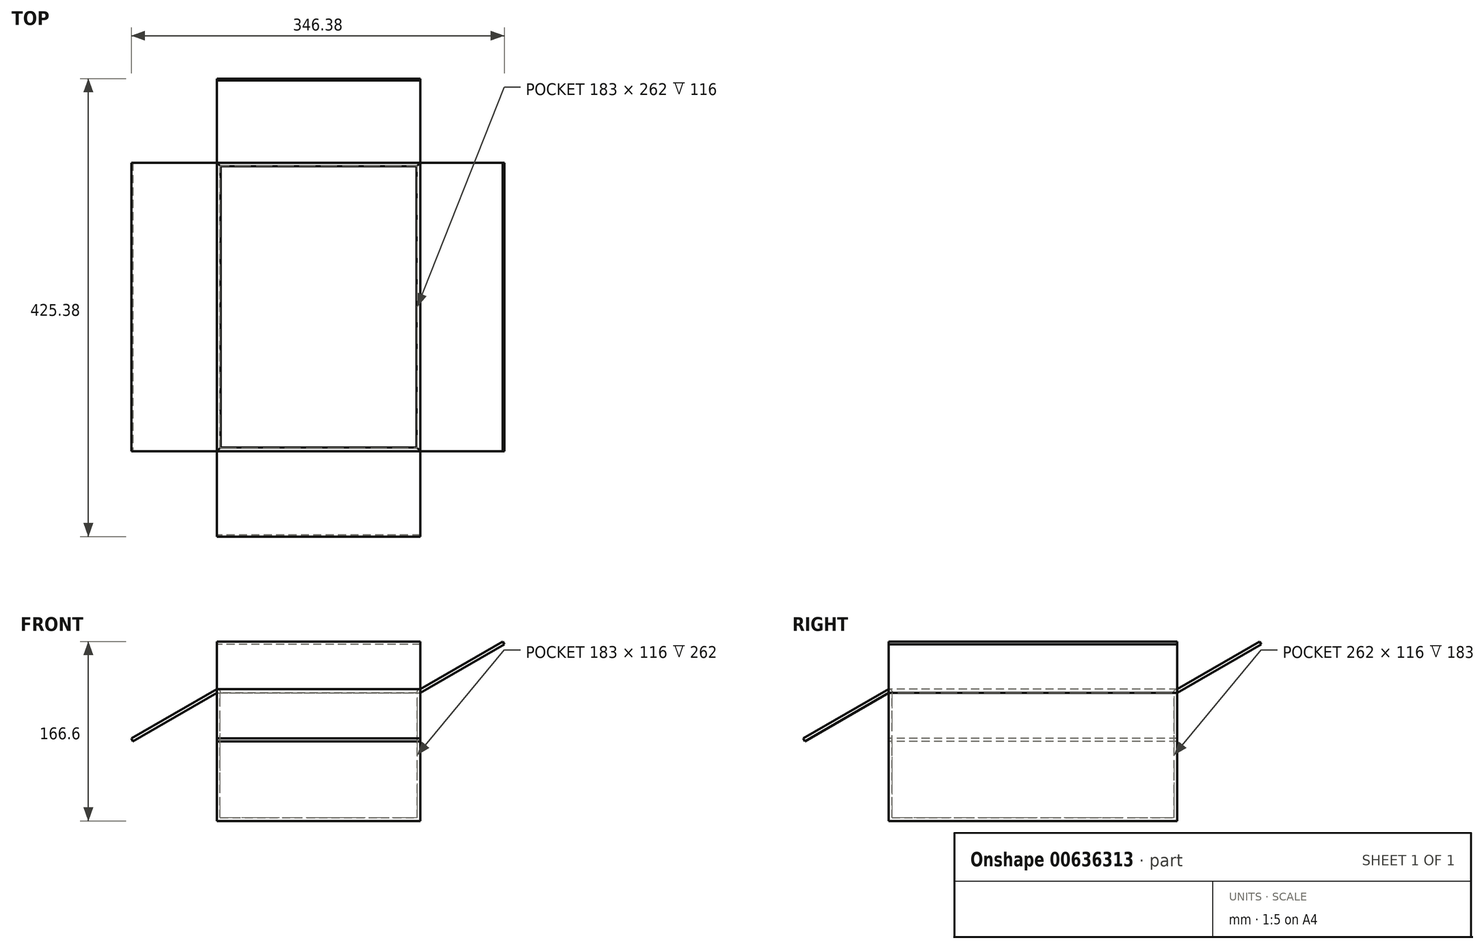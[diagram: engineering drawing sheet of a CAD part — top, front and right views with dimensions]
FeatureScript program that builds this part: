
annotation { "Feature Type Name" : "Feature", "Feature Type Description" : "" }
export const myFeature = defineFeature(function(context is Context, id is Id, definition is map)
    precondition{}
    {
        {
            var Q0;
            Q0=qCreatedBy(makeId("Front.planeOp"),FACE);
            var sketch = newSketch(context, id + "F0", { "sketchPlane" : qUnion([Q0])});
            skLineSegment(sketch, "E0.bottom", {"start": v(0, 0) * mm, "end": v(189, 0) * mm});
            skLineSegment(sketch, "E0.top", {"start": v(0, 119) * mm, "end": v(189, 119) * mm});
            skLineSegment(sketch, "E0.left", {"start": v(0, 0) * mm, "end": v(0, 119) * mm});
            skLineSegment(sketch, "E0.right", {"start": v(189, 0) * mm, "end": v(189, 119) * mm});
            skSolve(sketch);
        }
        {
            var Q0;
            Q0=qSketchRegion(id+"F0",true);
            extrude(context, id + "F1", {"entities" : qUnion([Q0]), "depth" : 268 * mm, "offsetDistance" : 25 * mm});
        }
        {
            var Q0;
            Q0=makeQuery(id+"F1.opExtrude","SWEPT_FACE",FACE,{"disambiguationData":[OSD([sQuery(id+"F0.wireOp",EDGE,"E0.top")])]});
            shell(context, id + "F2", {"entities" : qUnion([Q0]), "thickness" : 3 * mm});
        }
        {
            var Q0;
            Q0=makeQuery(id+"F1.opExtrude","CAP_FACE",FACE,{"disambiguationData":[OSD([sQuery(id+"F0.wireOp",EDGE,"E0.bottom"),sQuery(id+"F0.wireOp",EDGE,"E0.top"),sQuery(id+"F0.wireOp",EDGE,"E0.left"),sQuery(id+"F0.wireOp",EDGE,"E0.right")])],"isStart":false});
            var sketch = newSketch(context, id + "F3", { "sketchPlane" : qUnion([Q0])});
            skLineSegment(sketch, "E1", {"start": v(0, 119) * mm, "end": v(-77.94, 74) * mm});
            skLineSegment(sketch, "E2", {"start": v(-77.94, 74) * mm, "end": v(-79.44, 76.6) * mm});
            skLineSegment(sketch, "E3", {"start": v(-79.44, 76.6) * mm, "end": v(0, 122.46) * mm});
            skArc(sketch, "E4", {"start": v(0, 122.46) * mm, "mid": v(2.45, 121.45) * mm, "end": v(3.46, 119) * mm});
            skLineSegment(sketch, "E5", {"start": v(189, 119) * mm, "end": v(266.94, 164) * mm});
            skLineSegment(sketch, "E6", {"start": v(266.94, 164) * mm, "end": v(265.44, 166.6) * mm});
            skLineSegment(sketch, "E7", {"start": v(265.44, 166.6) * mm, "end": v(189, 122.46) * mm});
            skArc(sketch, "E8", {"start": v(189, 122.46) * mm, "mid": v(186.55, 121.45) * mm, "end": v(185.54, 119) * mm});
            skLineSegment(sketch, "E9", {"start": v(0, 119) * mm, "end": v(3.46, 119) * mm});
            skLineSegment(sketch, "E10", {"start": v(185.54, 119) * mm, "end": v(189, 119) * mm});
            skSolve(sketch);
        }
        {
            var Q0;
            Q0=qSketchRegion(id+"F3",true);
            var Q1;
            Q1=makeQuery(id+"F1.opExtrude","CAP_FACE",FACE,{"disambiguationData":[OSD([sQuery(id+"F0.wireOp",EDGE,"E0.bottom"),sQuery(id+"F0.wireOp",EDGE,"E0.top"),sQuery(id+"F0.wireOp",EDGE,"E0.left"),sQuery(id+"F0.wireOp",EDGE,"E0.right")])],"isStart":true});
            extrude(context, id + "F4", {"entities" : qUnion([Q0]), "operationType" : NewBodyOperationType.ADD, "endBound" : BoundingType.UP_TO_SURFACE, "oppositeDirection" : true, "depth" : 216 * mm, "endBoundEntityFace" : qUnion([Q1]), "offsetDistance" : 25 * mm});
        }
        {
            var Q0;
            Q0=makeQuery(id+"F1.opExtrude","SWEPT_FACE",FACE,{"disambiguationData":[OSD([sQuery(id+"F0.wireOp",EDGE,"E0.left")])]});
            var sketch = newSketch(context, id + "F5", { "sketchPlane" : qUnion([Q0])});
            skLineSegment(sketch, "E11", {"start": v(268, 119) * mm, "end": v(345.94, 74) * mm});
            skLineSegment(sketch, "E12", {"start": v(345.94, 74) * mm, "end": v(347.44, 76.6) * mm});
            skLineSegment(sketch, "E13", {"start": v(0, 119) * mm, "end": v(-77.94, 164) * mm});
            skLineSegment(sketch, "E14", {"start": v(-77.94, 164) * mm, "end": v(-76.44, 166.6) * mm});
            skLineSegment(sketch, "E15", {"start": v(-76.44, 166.6) * mm, "end": v(0, 122.46) * mm});
            skArc(sketch, "E16", {"start": v(0, 122.46) * mm, "mid": v(2.45, 121.45) * mm, "end": v(3.46, 119) * mm});
            skLineSegment(sketch, "E17", {"start": v(0, 119) * mm, "end": v(3.46, 119) * mm});
            skPoint(sketch, "E18.0", {"position": v(268, 122.46) * mm});
            skArc(sketch, "E19", {"start": v(268, 122.46) * mm, "mid": v(265.55, 121.45) * mm, "end": v(264.54, 119) * mm});
            skLineSegment(sketch, "E20", {"start": v(264.54, 119) * mm, "end": v(268, 119) * mm});
            skLineSegment(sketch, "E21", {"start": v(268, 122.46) * mm, "end": v(347.44, 76.6) * mm});
            skSolve(sketch);
        }
        {
            var Q0;
            Q0=qSketchRegion(id+"F5",true);
            var Q1;
            Q1=makeQuery(id+"F1.opExtrude","SWEPT_FACE",FACE,{"disambiguationData":[OSD([sQuery(id+"F0.wireOp",EDGE,"E0.right")])]});
            extrude(context, id + "F6", {"entities" : qUnion([Q0]), "operationType" : NewBodyOperationType.ADD, "endBound" : BoundingType.UP_TO_SURFACE, "oppositeDirection" : true, "depth" : 25 * mm, "endBoundEntityFace" : qUnion([Q1]), "offsetDistance" : 25 * mm});
        }
    });
